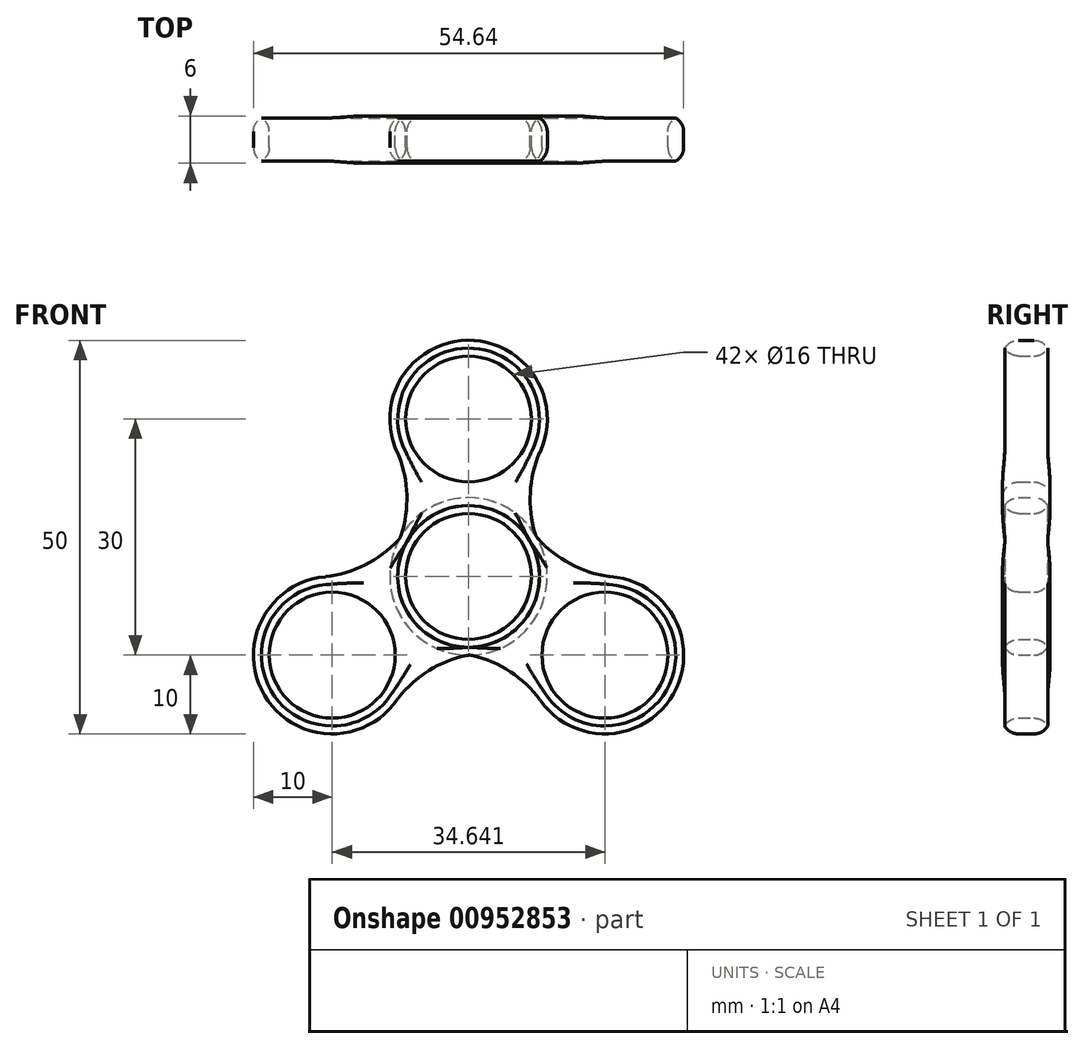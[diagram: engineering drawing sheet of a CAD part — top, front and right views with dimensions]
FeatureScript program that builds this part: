
annotation { "Feature Type Name" : "Feature", "Feature Type Description" : "" }
export const myFeature = defineFeature(function(context is Context, id is Id, definition is map)
    precondition{}
    {
        {
            var Q0;
            Q0=qCreatedBy(makeId("Front.planeOp"),FACE);
            var sketch = newSketch(context, id + "F0", { "sketchPlane" : qUnion([Q0])});
            skCircle(sketch, "E0", {"center": v(0, 0) * mm, "radius": 8 * mm});
            skCircle(sketch, "E1", {"center": v(0, 0) * mm, "radius": 10 * mm});
            skCircle(sketch, "E2", {"center": v(0, 20) * mm, "radius": 8 * mm});
            skCircle(sketch, "E3", {"center": v(0, 20) * mm, "radius": 10 * mm});
            skArc(sketch, "E4", {"start": v(-8.64, 5.03) * mm, "mid": v(-7.84, 10.3) * mm, "end": v(-8.93, 15.5) * mm});
            skArc(sketch, "E5", {"start": v(9.05, 15.75) * mm, "mid": v(7.83, 10.53) * mm, "end": v(8.53, 5.23) * mm});
            skSolve(sketch);
        }
        {
            var Q0;
            Q0 = qSketchRegion(id + "F0", true);
            extrude(context, id + "F1", {"entities" : qUnion([Q0]), "depth" : 6 * mm, "offsetDistance" : 25.4 * mm});
        }
        {
            var Q0;
            Q0=makeQuery(id+"F1.opExtrude","SWEPT_BODY",BODY,{"disambiguationData":[OSD([sQuery(id+"F0.wireOp",EDGE,"E0"),sQuery(id+"F0.wireOp",EDGE,"E1"),sQuery(id+"F0.wireOp",EDGE,"E2"),sQuery(id+"F0.wireOp",EDGE,"E3"),sQuery(id+"F0.wireOp",EDGE,"E4"),sQuery(id+"F0.wireOp",EDGE,"E5")])]});
            var Q1;
            Q1=makeQuery(id+"F1.opExtrude","SWEPT_FACE",FACE,{"disambiguationData":[OSD([sQuery(id+"F0.wireOp",EDGE,"E0")])]});
            circularPattern(context, id + "F2", {"entities" : qUnion([Q0]), "axis" : qUnion([Q1]), "angle" : 360 * degree, "instanceCount" : 3, "equalSpace" : true});
        }
        {
            var Q0;
            Q0=makeQuery(id+"F1.opExtrude","CAP_EDGE",EDGE,{"disambiguationData":[OSD([sQuery(id+"F0.wireOp",EDGE,"E3")])],"isStart":false});
            var Q1;
            Q1=makeQuery(id+"F1.opExtrude","SWEPT_FACE",FACE,{"disambiguationData":[OSD([sQuery(id+"F0.wireOp",EDGE,"E5")])]});
            var Q2;
            Q2=makeQuery(id+"F2.opPattern","COPY",EDGE,{"derivedFrom":makeQuery(id+"F1.opExtrude","CAP_EDGE",EDGE,{"disambiguationData":[OSD([sQuery(id+"F0.wireOp",EDGE,"E4")])],"isStart":false}),"instanceName":"2"});
            var Q3;
            Q3=makeQuery(id+"F2.opPattern","COPY",EDGE,{"derivedFrom":makeQuery(id+"F1.opExtrude","CAP_EDGE",EDGE,{"disambiguationData":[OSD([sQuery(id+"F0.wireOp",EDGE,"E3")])],"isStart":false}),"instanceName":"2"});
            var Q4;
            Q4=makeQuery(id+"F2.opPattern","COPY",EDGE,{"derivedFrom":makeQuery(id+"F1.opExtrude","CAP_EDGE",EDGE,{"disambiguationData":[OSD([sQuery(id+"F0.wireOp",EDGE,"E5")])],"isStart":false}),"instanceName":"2"});
            var Q5;
            Q5=makeQuery(id+"F1.opExtrude","CAP_EDGE",EDGE,{"disambiguationData":[OSD([sQuery(id+"F0.wireOp",EDGE,"E0")])],"isStart":false});
            var Q6;
            Q6=makeQuery(id+"F2.opPattern","COPY",EDGE,{"derivedFrom":makeQuery(id+"F1.opExtrude","CAP_EDGE",EDGE,{"disambiguationData":[OSD([sQuery(id+"F0.wireOp",EDGE,"E5")])],"isStart":false}),"instanceName":"1"});
            var Q7;
            Q7=makeQuery(id+"F1.opExtrude","CAP_EDGE",EDGE,{"disambiguationData":[OSD([sQuery(id+"F0.wireOp",EDGE,"E4")])],"isStart":false});
            var Q8;
            Q8=makeQuery(id+"F2.opPattern","COPY",EDGE,{"derivedFrom":makeQuery(id+"F1.opExtrude","CAP_EDGE",EDGE,{"disambiguationData":[OSD([sQuery(id+"F0.wireOp",EDGE,"E3")])],"isStart":false}),"instanceName":"1"});
            var Q9;
            Q9=makeQuery(id+"F2.opPattern","COPY",EDGE,{"derivedFrom":makeQuery(id+"F1.opExtrude","CAP_EDGE",EDGE,{"disambiguationData":[OSD([sQuery(id+"F0.wireOp",EDGE,"E4")])],"isStart":false}),"instanceName":"1"});
            var Q10;
            Q10=makeQuery(id+"F2.opPattern","COPY",EDGE,{"derivedFrom":makeQuery(id+"F1.opExtrude","CAP_EDGE",EDGE,{"disambiguationData":[OSD([sQuery(id+"F0.wireOp",EDGE,"E4")])],"isStart":true}),"instanceName":"2"});
            var Q11;
            Q11=makeQuery(id+"F2.opPattern","COPY",EDGE,{"derivedFrom":makeQuery(id+"F1.opExtrude","CAP_EDGE",EDGE,{"disambiguationData":[OSD([sQuery(id+"F0.wireOp",EDGE,"E3")])],"isStart":true}),"instanceName":"2"});
            var Q12;
            Q12=makeQuery(id+"F2.opPattern","COPY",EDGE,{"derivedFrom":makeQuery(id+"F1.opExtrude","CAP_EDGE",EDGE,{"disambiguationData":[OSD([sQuery(id+"F0.wireOp",EDGE,"E1")])],"isStart":false}),"instanceName":"1"});
            var Q13;
            Q13=makeQuery(id+"F1.opExtrude","CAP_EDGE",EDGE,{"disambiguationData":[OSD([sQuery(id+"F0.wireOp",EDGE,"E5")])],"isStart":true});
            var Q14;
            Q14=makeQuery(id+"F1.opExtrude","CAP_EDGE",EDGE,{"disambiguationData":[OSD([sQuery(id+"F0.wireOp",EDGE,"E5")])],"isStart":false});
            var Q15;
            Q15=makeQuery(id+"F1.opExtrude","SWEPT_EDGE",EDGE,{"disambiguationData":[OSD([sQuery(id+"F0.wireOp",EDGE,"E3"),sQuery(id+"F0.wireOp",EDGE,"E5")])]});
            var Q16;
            Q16=makeQuery(id+"F1.opExtrude","CAP_EDGE",EDGE,{"disambiguationData":[OSD([sQuery(id+"F0.wireOp",EDGE,"E2")])],"isStart":false});
            var Q17;
            Q17=makeQuery(id+"F1.opExtrude","CAP_EDGE",EDGE,{"disambiguationData":[OSD([sQuery(id+"F0.wireOp",EDGE,"E3")])],"isStart":true});
            var Q18;
            Q18=makeQuery(id+"F2.opPattern","COPY",EDGE,{"derivedFrom":makeQuery(id+"F1.opExtrude","CAP_EDGE",EDGE,{"disambiguationData":[OSD([sQuery(id+"F0.wireOp",EDGE,"E0")])],"isStart":false}),"instanceName":"1"});
            var Q19;
            Q19=makeQuery(id+"F2.opPattern","COPY",EDGE,{"derivedFrom":makeQuery(id+"F1.opExtrude","CAP_EDGE",EDGE,{"disambiguationData":[OSD([sQuery(id+"F0.wireOp",EDGE,"E1")])],"isStart":true}),"instanceName":"1"});
            var Q20;
            Q20=makeQuery(id+"F1.opExtrude","SWEPT_EDGE",EDGE,{"disambiguationData":[OSD([sQuery(id+"F0.wireOp",EDGE,"E1"),sQuery(id+"F0.wireOp",EDGE,"E5")])]});
            var Q21;
            Q21=makeQuery(id+"F1.opExtrude","CAP_EDGE",EDGE,{"disambiguationData":[OSD([sQuery(id+"F0.wireOp",EDGE,"E0")])],"isStart":true});
            var Q22;
            Q22=makeQuery(id+"F1.opExtrude","CAP_EDGE",EDGE,{"disambiguationData":[OSD([sQuery(id+"F0.wireOp",EDGE,"E1")])],"isStart":true});
            var Q23;
            Q23=makeQuery(id+"F1.opExtrude","CAP_EDGE",EDGE,{"disambiguationData":[OSD([sQuery(id+"F0.wireOp",EDGE,"E1")])],"isStart":false});
            var Q24;
            Q24=makeQuery(id+"F1.opExtrude","CAP_EDGE",EDGE,{"disambiguationData":[OSD([sQuery(id+"F0.wireOp",EDGE,"E2")])],"isStart":true});
            var Q25;
            Q25=makeQuery(id+"F2.opPattern","COPY",EDGE,{"derivedFrom":makeQuery(id+"F1.opExtrude","SWEPT_EDGE",EDGE,{"disambiguationData":[OSD([sQuery(id+"F0.wireOp",EDGE,"E1"),sQuery(id+"F0.wireOp",EDGE,"E4")])]}),"instanceName":"2"});
            var Q26;
            Q26=makeQuery(id+"F2.opPattern","COPY",EDGE,{"derivedFrom":makeQuery(id+"F1.opExtrude","SWEPT_EDGE",EDGE,{"disambiguationData":[OSD([sQuery(id+"F0.wireOp",EDGE,"E3"),sQuery(id+"F0.wireOp",EDGE,"E4")])]}),"instanceName":"2"});
            var Q27;
            Q27=makeQuery(id+"F2.opPattern","COPY",EDGE,{"derivedFrom":makeQuery(id+"F1.opExtrude","CAP_EDGE",EDGE,{"disambiguationData":[OSD([sQuery(id+"F0.wireOp",EDGE,"E1")])],"isStart":true}),"instanceName":"2"});
            var Q28;
            Q28=makeQuery(id+"F2.opPattern","COPY",EDGE,{"derivedFrom":makeQuery(id+"F1.opExtrude","CAP_EDGE",EDGE,{"disambiguationData":[OSD([sQuery(id+"F0.wireOp",EDGE,"E1")])],"isStart":false}),"instanceName":"2"});
            var Q29;
            Q29=makeQuery(id+"F2.opPattern","COPY",EDGE,{"derivedFrom":makeQuery(id+"F1.opExtrude","CAP_EDGE",EDGE,{"disambiguationData":[OSD([sQuery(id+"F0.wireOp",EDGE,"E0")])],"isStart":true}),"instanceName":"1"});
            var Q30;
            Q30=makeQuery(id+"F2.opPattern","COPY",EDGE,{"derivedFrom":makeQuery(id+"F1.opExtrude","CAP_EDGE",EDGE,{"disambiguationData":[OSD([sQuery(id+"F0.wireOp",EDGE,"E0")])],"isStart":false}),"instanceName":"2"});
            var Q31;
            Q31=makeQuery(id+"F2.opPattern","COPY",EDGE,{"derivedFrom":makeQuery(id+"F1.opExtrude","CAP_EDGE",EDGE,{"disambiguationData":[OSD([sQuery(id+"F0.wireOp",EDGE,"E0")])],"isStart":true}),"instanceName":"2"});
            var Q32;
            Q32=makeQuery(id+"F2.opPattern","COPY",EDGE,{"derivedFrom":makeQuery(id+"F1.opExtrude","CAP_EDGE",EDGE,{"disambiguationData":[OSD([sQuery(id+"F0.wireOp",EDGE,"E5")])],"isStart":true}),"instanceName":"1"});
            var Q33;
            Q33=makeQuery(id+"F2.opPattern","COPY",EDGE,{"derivedFrom":makeQuery(id+"F1.opExtrude","SWEPT_EDGE",EDGE,{"disambiguationData":[OSD([sQuery(id+"F0.wireOp",EDGE,"E3"),sQuery(id+"F0.wireOp",EDGE,"E5")])]}),"instanceName":"1"});
            var Q34;
            Q34=makeQuery(id+"F2.opPattern","COPY",EDGE,{"derivedFrom":makeQuery(id+"F1.opExtrude","CAP_EDGE",EDGE,{"disambiguationData":[OSD([sQuery(id+"F0.wireOp",EDGE,"E2")])],"isStart":true}),"instanceName":"1"});
            var Q35;
            Q35=makeQuery(id+"F2.opPattern","COPY",EDGE,{"derivedFrom":makeQuery(id+"F1.opExtrude","CAP_EDGE",EDGE,{"disambiguationData":[OSD([sQuery(id+"F0.wireOp",EDGE,"E2")])],"isStart":false}),"instanceName":"1"});
            var Q36;
            Q36=makeQuery(id+"F2.opPattern","COPY",EDGE,{"derivedFrom":makeQuery(id+"F1.opExtrude","CAP_EDGE",EDGE,{"disambiguationData":[OSD([sQuery(id+"F0.wireOp",EDGE,"E3")])],"isStart":true}),"instanceName":"1"});
            var Q37;
            Q37=makeQuery(id+"F2.opPattern","COPY",EDGE,{"derivedFrom":makeQuery(id+"F1.opExtrude","CAP_EDGE",EDGE,{"disambiguationData":[OSD([sQuery(id+"F0.wireOp",EDGE,"E2")])],"isStart":true}),"instanceName":"2"});
            var Q38;
            Q38=makeQuery(id+"F2.opPattern","COPY",EDGE,{"derivedFrom":makeQuery(id+"F1.opExtrude","CAP_EDGE",EDGE,{"disambiguationData":[OSD([sQuery(id+"F0.wireOp",EDGE,"E2")])],"isStart":false}),"instanceName":"2"});
            var Q39;
            Q39=makeQuery(id+"F2.opPattern","COPY",EDGE,{"derivedFrom":makeQuery(id+"F1.opExtrude","SWEPT_EDGE",EDGE,{"disambiguationData":[OSD([sQuery(id+"F0.wireOp",EDGE,"E3"),sQuery(id+"F0.wireOp",EDGE,"E4")])]}),"instanceName":"1"});
            var Q40;
            Q40=makeQuery(id+"F2.opPattern","COPY",EDGE,{"derivedFrom":makeQuery(id+"F1.opExtrude","SWEPT_EDGE",EDGE,{"disambiguationData":[OSD([sQuery(id+"F0.wireOp",EDGE,"E1"),sQuery(id+"F0.wireOp",EDGE,"E5")])]}),"instanceName":"1"});
            var Q41;
            Q41=makeQuery(id+"F2.opPattern","COPY",EDGE,{"derivedFrom":makeQuery(id+"F1.opExtrude","CAP_EDGE",EDGE,{"disambiguationData":[OSD([sQuery(id+"F0.wireOp",EDGE,"E4")])],"isStart":true}),"instanceName":"1"});
            var Q42;
            Q42=makeQuery(id+"F1.opExtrude","SWEPT_EDGE",EDGE,{"disambiguationData":[OSD([sQuery(id+"F0.wireOp",EDGE,"E1"),sQuery(id+"F0.wireOp",EDGE,"E4")])]});
            var Q43;
            Q43=makeQuery(id+"F1.opExtrude","SWEPT_EDGE",EDGE,{"disambiguationData":[OSD([sQuery(id+"F0.wireOp",EDGE,"E3"),sQuery(id+"F0.wireOp",EDGE,"E4")])]});
            var Q44;
            Q44=makeQuery(id+"F1.opExtrude","CAP_EDGE",EDGE,{"disambiguationData":[OSD([sQuery(id+"F0.wireOp",EDGE,"E4")])],"isStart":true});
            var Q45;
            Q45=makeQuery(id+"F2.opPattern","COPY",EDGE,{"derivedFrom":makeQuery(id+"F1.opExtrude","CAP_EDGE",EDGE,{"disambiguationData":[OSD([sQuery(id+"F0.wireOp",EDGE,"E5")])],"isStart":true}),"instanceName":"2"});
            var Q46;
            Q46=makeQuery(id+"F2.opPattern","COPY",EDGE,{"derivedFrom":makeQuery(id+"F1.opExtrude","SWEPT_EDGE",EDGE,{"disambiguationData":[OSD([sQuery(id+"F0.wireOp",EDGE,"E3"),sQuery(id+"F0.wireOp",EDGE,"E5")])]}),"instanceName":"2"});
            var Q47;
            Q47=makeQuery(id+"F2.opPattern","COPY",EDGE,{"derivedFrom":makeQuery(id+"F1.opExtrude","SWEPT_EDGE",EDGE,{"disambiguationData":[OSD([sQuery(id+"F0.wireOp",EDGE,"E1"),sQuery(id+"F0.wireOp",EDGE,"E5")])]}),"instanceName":"2"});
            var Q48;
            Q48=makeQuery(id+"F2.opPattern","COPY",EDGE,{"derivedFrom":makeQuery(id+"F1.opExtrude","SWEPT_EDGE",EDGE,{"disambiguationData":[OSD([sQuery(id+"F0.wireOp",EDGE,"E1"),sQuery(id+"F0.wireOp",EDGE,"E4")])]}),"instanceName":"1"});
            fillet(context, id + "F3", {"entities" : qUnion([Q0, Q1, Q2, Q3, Q4, Q5, Q6, Q7, Q8, Q9, Q10, Q11, Q12, Q13, Q14, Q15, Q16, Q17, Q18, Q19, Q20, Q21, Q22, Q23, Q24, Q25, Q26, Q27, Q28, Q29, Q30, Q31, Q32, Q33, Q34, Q35, Q36, Q37, Q38, Q39, Q40, Q41, Q42, Q43, Q44, Q45, Q46, Q47, Q48]), "radius" : 2 * mm, "tangentPropagation" : true, "allowEdgeOverflow" : false});
        }
    });
